# Revit family: Crealco Pivot 38 Horizontal Opening
name_source: partatom
category: Windows
revit_build: Autodesk Revit 2016 (Build: 20150714_1515(x64)
units: mm (PartAtom-declared; Revit-internal decimal feet)

## family parameters
Always vertical = Yes
Cut with Voids When Loaded = No
Host = Wall
OmniClass Number = 23.30.20.00
OmniClass Title = Windows
Room Calculation Point = No
Shared = No

## types (13) — shared parameters
DG Thickness Max = 25 mm  [stored 0.082021 ft]
DG Thickness Min = 20 mm  [stored 0.0656168 ft]
Default Sill Height = 800 mm  [stored 2.62467 ft]
Description = Horizontal Pivot Window
Limit Sash Height Max = 1500 mm  [stored 4.92126 ft]
Limit Sash Height Min = 200 mm  [stored 0.656168 ft]
Limit Sash Width Max = 1200 mm
Limit Sash Width Min = 200 mm  [stored 0.656168 ft]
Limit Window Height Max = 1594 mm  [stored 5.22966 ft]
Limit Window Height Min = 294 mm
Limit Window Width Max = 1294 mm  [stored 4.24541 ft]
Limit Window Width Min = 294 mm
Manufacturer = Crealco
Model = Pivot 38 Window
SG Thickness Max = 10 mm  [stored 0.0328084 ft]
SG Thickness Min = 4 mm  [stored 0.0131234 ft]
Sash Side Gap = 47 mm  [stored 0.154199 ft]
URL = https://www.crealco.co.za
Wall Closure = By host

## per-type parameters (varying)
| type | Standard Height | Standard Size | Standard Width | Type Comments |
| 0590 x 0590mm (P38-0606H) | 590 mm  [stored 1.9357 ft] | Yes | 590 mm  [stored 1.9357 ft] | P38-0606H |
| User Defined | 590 mm  [stored 1.9357 ft] | No | 590 mm  [stored 1.9357 ft] | P38H-Custom |
| 0590 x 0890mm (P38-0609H) | 890 mm  [stored 2.91995 ft] | Yes | 590 mm  [stored 1.9357 ft] | P38-0609H |
| 0590 x 1190mm (P38-0612H) | 1190 mm  [stored 3.9042 ft] | Yes | 590 mm  [stored 1.9357 ft] | P38-06012H |
| 0590 x 1490mm (P38-0615H) | 1490 mm  [stored 4.88845 ft] | Yes | 590 mm  [stored 1.9357 ft] | P38-0615H |
| 0890 x 0590mm (P38-0906H) | 590 mm  [stored 1.9357 ft] | Yes | 890 mm  [stored 2.91995 ft] | P38-0906H |
| 1190 x 0590mm (P38-1206H) | 590 mm  [stored 1.9357 ft] | Yes | 1190 mm  [stored 3.9042 ft] | P38-1206H |
| 0890 x 0890mm (P38-0909H) | 890 mm  [stored 2.91995 ft] | Yes | 890 mm  [stored 2.91995 ft] | P38-0909H |
| 0890 x 1190mm (P38-0912H) | 1190 mm  [stored 3.9042 ft] | Yes | 890 mm  [stored 2.91995 ft] | P38-0912H |
| 0890 x 1490mm (P38-0915H) | 1490 mm  [stored 4.88845 ft] | Yes | 890 mm  [stored 2.91995 ft] | P38-0915H |
| 1190 x 0890mm (P38-1209H) | 890 mm  [stored 2.91995 ft] | Yes | 1190 mm  [stored 3.9042 ft] | P38-1209H |
| 1190 x 1190mm (P38-1212H) | 1190 mm  [stored 3.9042 ft] | Yes | 1190 mm  [stored 3.9042 ft] | P38-1212H |
| 1190 x 1490mm (P38-1215H) | 1490 mm  [stored 4.88845 ft] | Yes | 1190 mm  [stored 3.9042 ft] | P38-1215H |

note: [stored X ft] marks values corroborated as IEEE doubles in the binary element streams (Revit-internal decimal feet)

## geometry (parser evidence)
native form markers: Sweep x20
no freeform markers — native parametric forms only
